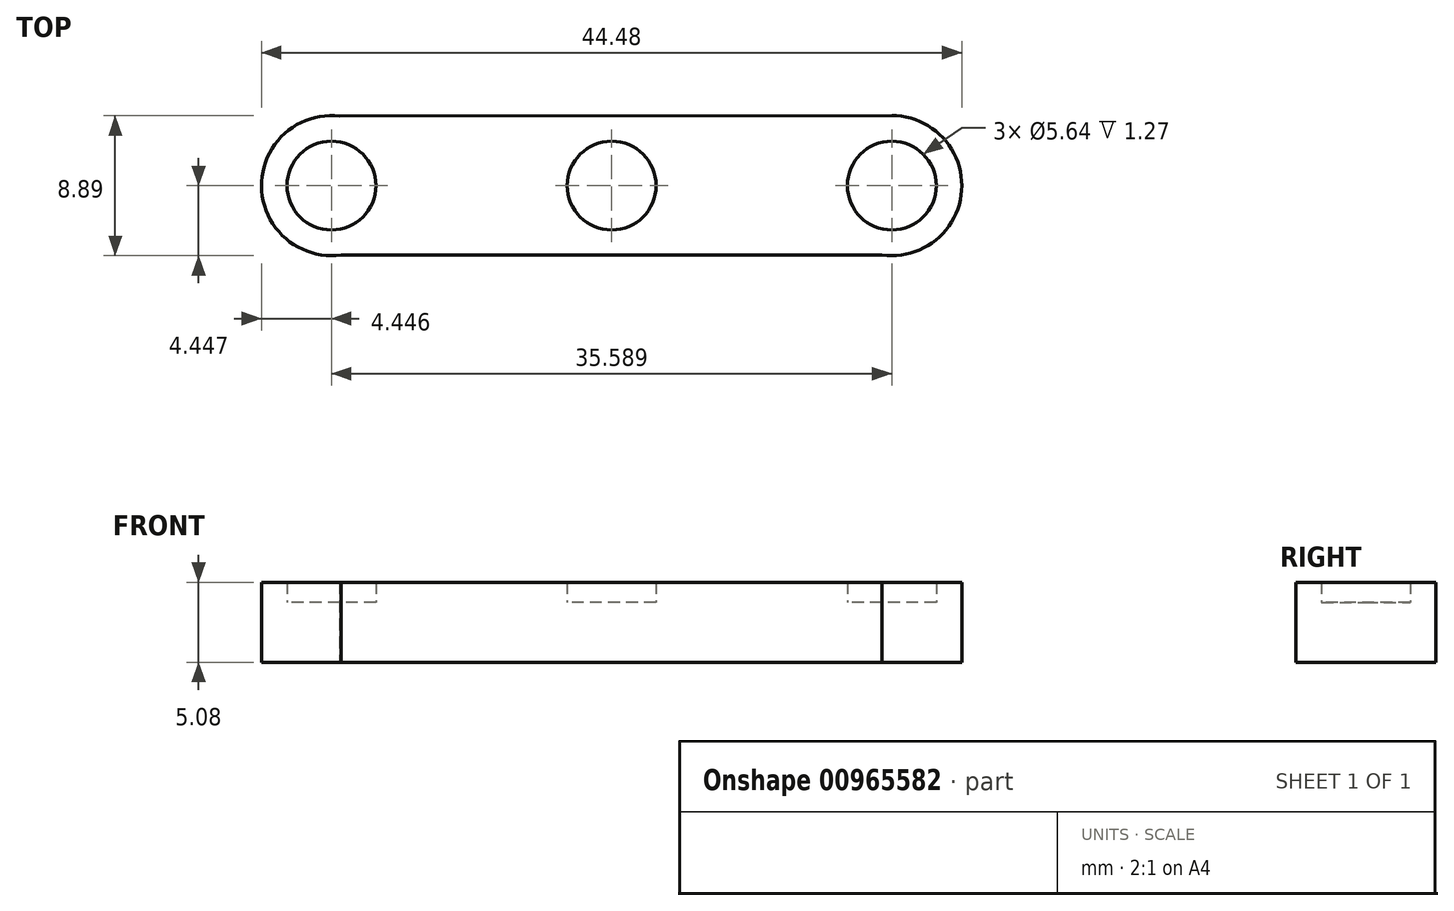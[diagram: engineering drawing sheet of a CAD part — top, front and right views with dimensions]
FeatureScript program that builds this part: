
annotation { "Feature Type Name" : "Feature", "Feature Type Description" : "" }
export const myFeature = defineFeature(function(context is Context, id is Id, definition is map)
    precondition{}
    {
        {
            var Q0;
            Q0=qCreatedBy(makeId("Top.planeOp"),FACE);
            var sketch = newSketch(context, id + "F0", { "sketchPlane" : qUnion([Q0])});
            skCircle(sketch, "E0", {"center": v(-28.3, 23.5) * mm, "radius": 4.45 * mm});
            skCircle(sketch, "E1", {"center": v(-63.88, 23.5) * mm, "radius": 4.45 * mm});
            skLineSegment(sketch, "E2", {"start": v(-64.41, 27.92) * mm, "end": v(-28.3, 27.95) * mm});
            skLineSegment(sketch, "E3", {"start": v(-64.5, 19.1) * mm, "end": v(-27.68, 19.1) * mm});
            skCircle(sketch, "E4", {"center": v(-28.3, 23.5) * mm, "radius": 2.82 * mm});
            skCircle(sketch, "E5", {"center": v(-46.09, 23.5) * mm, "radius": 2.82 * mm});
            skCircle(sketch, "E6", {"center": v(-63.88, 23.5) * mm, "radius": 2.82 * mm});
            skSolve(sketch);
        }
        {
            var Q0;
            Q0 = qSketchRegion(id + "F0", true);
            extrude(context, id + "F1", {"entities" : qUnion([Q0]), "depth" : 5.08 * mm, "offsetDistance" : 25.4 * mm});
        }
        {
            var Q0;
            Q0=makeQuery(id+"F0.imprint","IMPRINT",FACE,{"disambiguationData":[TD([[makeQuery(id+"F0.imprint","IMPRINT",EDGE,{"derivedFrom":sQuery(id+"F0.wireOp",EDGE,"E4")}),1.0]])]});
            var Q1;
            Q1=makeQuery(id+"F0.imprint","IMPRINT",FACE,{"disambiguationData":[TD([[makeQuery(id+"F0.imprint","IMPRINT",EDGE,{"derivedFrom":sQuery(id+"F0.wireOp",EDGE,"E5")}),1.0]])]});
            var Q2;
            Q2=makeQuery(id+"F0.imprint","IMPRINT",FACE,{"disambiguationData":[TD([[makeQuery(id+"F0.imprint","IMPRINT",EDGE,{"derivedFrom":sQuery(id+"F0.wireOp",EDGE,"E6")}),1.0]])]});
            extrude(context, id + "F2", {"entities" : qUnion([Q0, Q1, Q2]), "operationType" : NewBodyOperationType.ADD, "depth" : 3.8 * mm, "offsetDistance" : 25.4 * mm});
        }
    });
